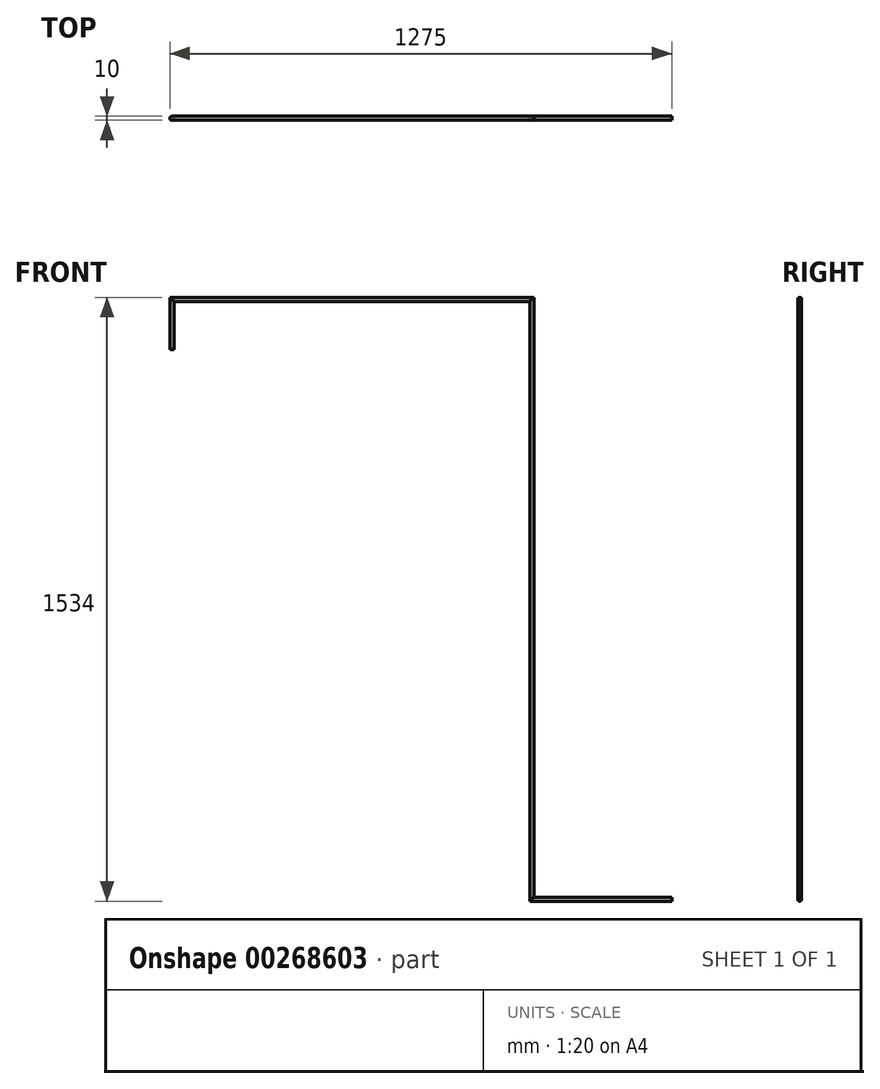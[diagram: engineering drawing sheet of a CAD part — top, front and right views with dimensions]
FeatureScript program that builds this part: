
annotation { "Feature Type Name" : "Feature", "Feature Type Description" : "" }
export const myFeature = defineFeature(function(context is Context, id is Id, definition is map)
    precondition{}
    {
        {
            var Q0;
            Q0=qCreatedBy(makeId("Top.planeOp"),FACE);
            var sketch = newSketch(context, id + "F0", { "sketchPlane" : qUnion([Q0])});
            skCircle(sketch, "E0", {"center": v(0, 0) * mm, "radius": 5 * mm});
            skSolve(sketch);
        }
        {
            var Q0;
            Q0=qCreatedBy(makeId("Front.planeOp"),FACE);
            var sketch = newSketch(context, id + "F1", { "sketchPlane" : qUnion([Q0])});
            skLineSegment(sketch, "E1", {"start": v(0, 0) * mm, "end": v(0, 127) * mm});
            skLineSegment(sketch, "E2", {"start": v(0, 127) * mm, "end": v(914.4, 127) * mm});
            skLineSegment(sketch, "E3", {"start": v(914.4, 127) * mm, "end": v(914.4, -1397) * mm});
            skLineSegment(sketch, "E4", {"start": v(914.4, -1397) * mm, "end": v(1270, -1397) * mm});
            skSolve(sketch);
        }
        {
            var Q0;
            Q0=makeQuery(id+"F0.imprint","IMPRINT",FACE,{"disambiguationData":[TD([[makeQuery(id+"F0.imprint","IMPRINT",EDGE,{"derivedFrom":sQuery(id+"F0.wireOp",EDGE,"E0")}),1.0]])]});
            var Q1;
            Q1=sQuery(id+"F1.wireOp",EDGE,"E1");
            var Q2;
            Q2=sQuery(id+"F1.wireOp",EDGE,"E2");
            var Q3;
            Q3=sQuery(id+"F1.wireOp",EDGE,"E3");
            var Q4;
            Q4=sQuery(id+"F1.wireOp",EDGE,"E4");
            sweep(context, id + "F2", {"profiles" : qUnion([Q0]), "path" : qUnion([Q1, Q2, Q3, Q4])});
        }
    });
